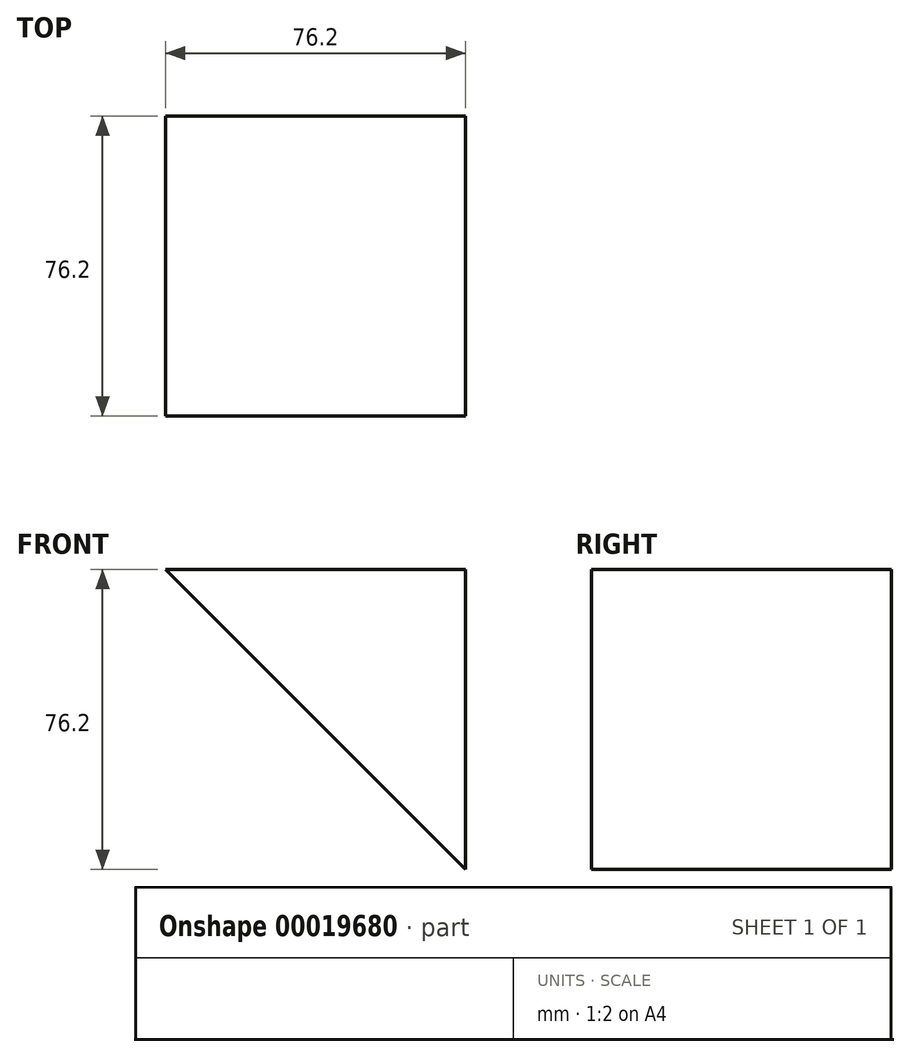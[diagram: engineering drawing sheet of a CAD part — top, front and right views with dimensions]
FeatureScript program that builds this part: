
annotation { "Feature Type Name" : "Feature", "Feature Type Description" : "" }
export const myFeature = defineFeature(function(context is Context, id is Id, definition is map)
    precondition{}
    {
        {
            var Q0;
            Q0=qCreatedBy(makeId("Front.planeOp"),FACE);
            var sketch = newSketch(context, id + "F0", { "sketchPlane" : qUnion([Q0])});
            skLineSegment(sketch, "E0", {"start": v(0, 0) * mm, "end": v(0, 76.2) * mm});
            skLineSegment(sketch, "E1", {"start": v(0, 76.2) * mm, "end": v(76.2, 76.2) * mm});
            skLineSegment(sketch, "E2", {"start": v(76.2, 76.2) * mm, "end": v(76.2, 0) * mm});
            skLineSegment(sketch, "E3", {"start": v(0, 0) * mm, "end": v(76.2, 0) * mm});
            skLineSegment(sketch, "E4", {"start": v(0, 76.2) * mm, "end": v(76.2, 0) * mm});
            skSolve(sketch);
        }
        {
            var Q0;
            Q0=makeQuery(id+"F0.imprint","IMPRINT",FACE,{"disambiguationData":[TD([[makeQuery(id+"F0.imprint","IMPRINT",EDGE,{"derivedFrom":sQuery(id+"F0.wireOp",EDGE,"E1")}),-1.0]])]});
            extrude(context, id + "F1", {"entities" : qUnion([Q0]), "depth" : 76.2 * mm});
        }
    });
